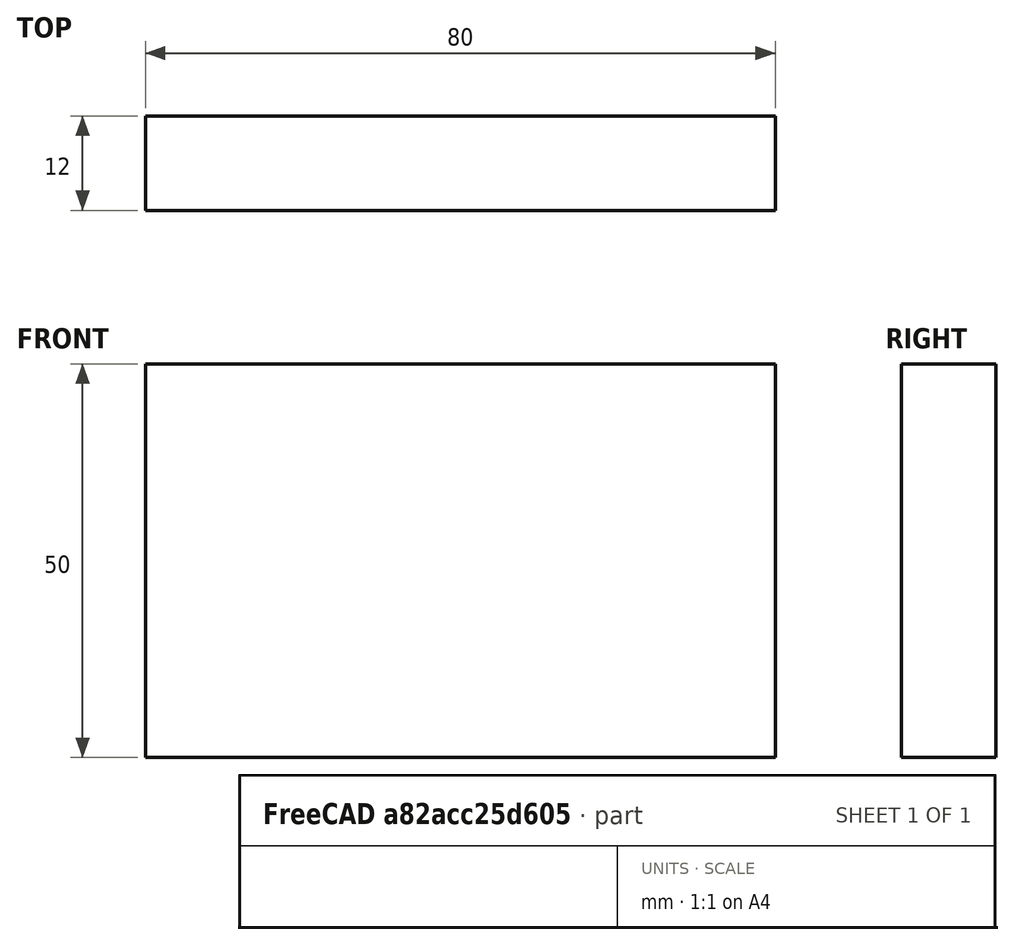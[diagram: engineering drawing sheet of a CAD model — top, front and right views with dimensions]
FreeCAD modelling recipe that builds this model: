
FCSTD DOCUMENT  (FreeCAD 0.15R4671 (Git))
Label: Flat Bar 80x12 EN10058 S235JR
License: All rights reserved
LicenseURL: http://en.wikipedia.org/wiki/All_rights_reserved
objects: Sketcher::SketchObject×1, Part::Extrusion×1
note: 2 computed .brp shape members not serialized (recipe doc carries the construction recipe); baked Part::Feature solids carry a one-line shape summary decoded from their .brp

FEATURE [Sketcher::SketchObject] Sketch
  sketch-geometry (4):
    g0: LineSegment StartX=-40 StartY=-6 StartZ=0 EndX=40 EndY=-6 EndZ=0
    g1: LineSegment StartX=40 StartY=-6 StartZ=0 EndX=40 EndY=6 EndZ=0
    g2: LineSegment StartX=40 StartY=6 StartZ=0 EndX=-40 EndY=6 EndZ=0
    g3: LineSegment StartX=-40 StartY=6 StartZ=0 EndX=-40 EndY=-6 EndZ=0
  constraints (12):
    c: Coincident(g0,g1)
    c: Coincident(g1,g2)
    c: Coincident(g2,g3)
    c: Coincident(g3,g0)
    c: Horizontal(g0)
    c: Horizontal(g2)
    c: Vertical(g1)
    c: Vertical(g3)
    c: Symmetric(g1,g2,g-2)
    c: Symmetric(g0,g1,g-1)
    c: DistanceY(g1) = 12
    c: DistanceX(g0) = 80
FEATURE [Part::Extrusion] Extrude  label="Flat Bar 80x12 EN10058 S235JR"
  Base = -> Sketch
  Dir = (0,0,50)
  Solid = true
